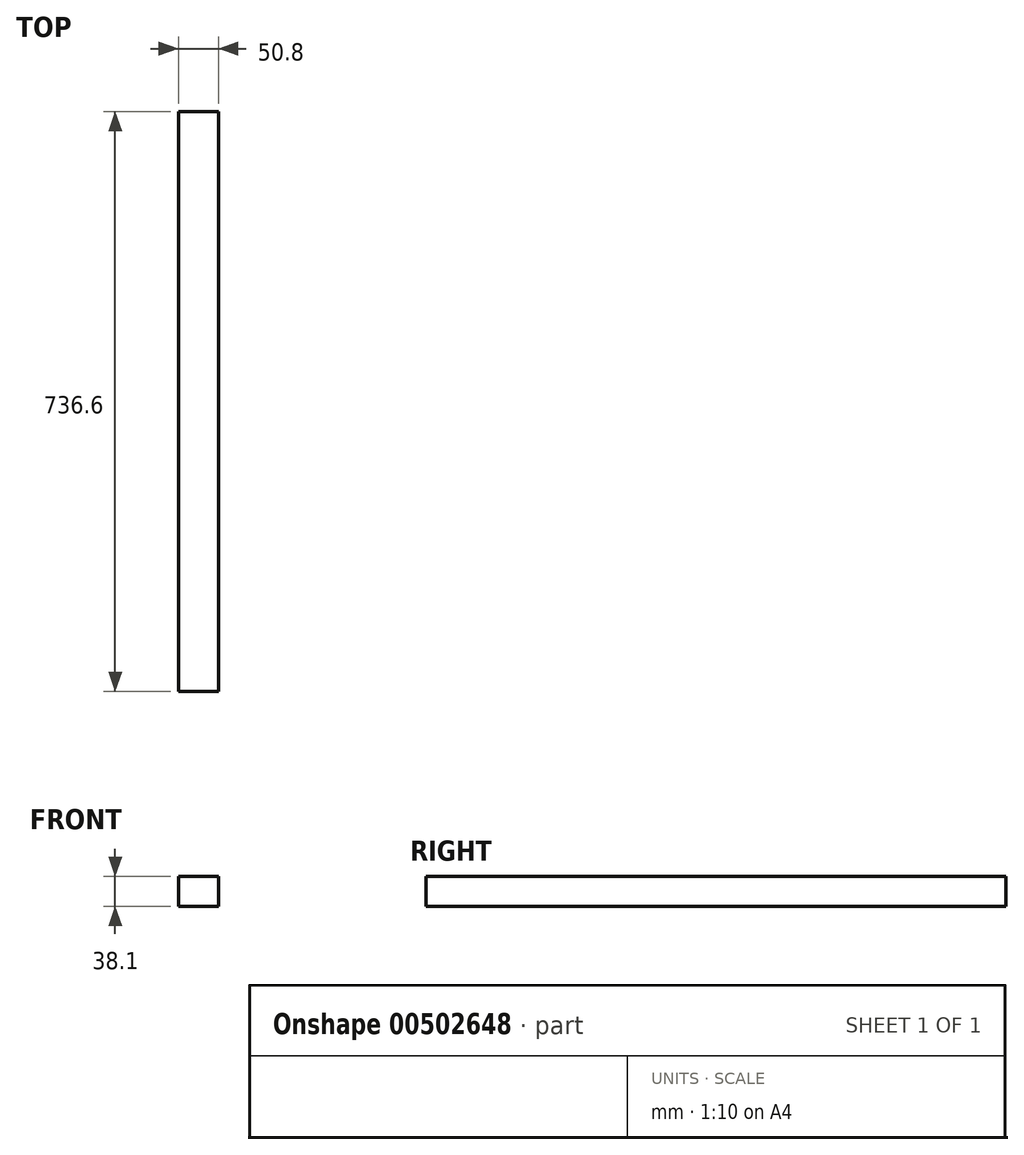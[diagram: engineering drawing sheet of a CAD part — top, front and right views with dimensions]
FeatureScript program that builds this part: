
annotation { "Feature Type Name" : "Feature", "Feature Type Description" : "" }
export const myFeature = defineFeature(function(context is Context, id is Id, definition is map)
    precondition{}
    {
        {
            var Q0;
            Q0=qCreatedBy(makeId("Front.planeOp"),FACE);
            var sketch = newSketch(context, id + "F0", { "sketchPlane" : qUnion([Q0])});
            skLineSegment(sketch, "E0.bottom", {"start": v(0, 0) * mm, "end": v(50.8, 0) * mm});
            skLineSegment(sketch, "E0.top", {"start": v(0, 38.1) * mm, "end": v(50.8, 38.1) * mm});
            skLineSegment(sketch, "E0.left", {"start": v(0, 0) * mm, "end": v(0, 38.1) * mm});
            skLineSegment(sketch, "E0.right", {"start": v(50.8, 0) * mm, "end": v(50.8, 38.1) * mm});
            skSolve(sketch);
        }
        {
            var Q0;
            Q0=makeQuery(id+"F0.imprint","IMPRINT",FACE,{"disambiguationData":[TD([[makeQuery(id+"F0.imprint","IMPRINT",EDGE,{"derivedFrom":sQuery(id+"F0.wireOp",EDGE,"E0.bottom")}),1.0]])]});
            extrude(context, id + "F1", {"entities" : qUnion([Q0]), "depth" : 736.6 * mm});
        }
    });
